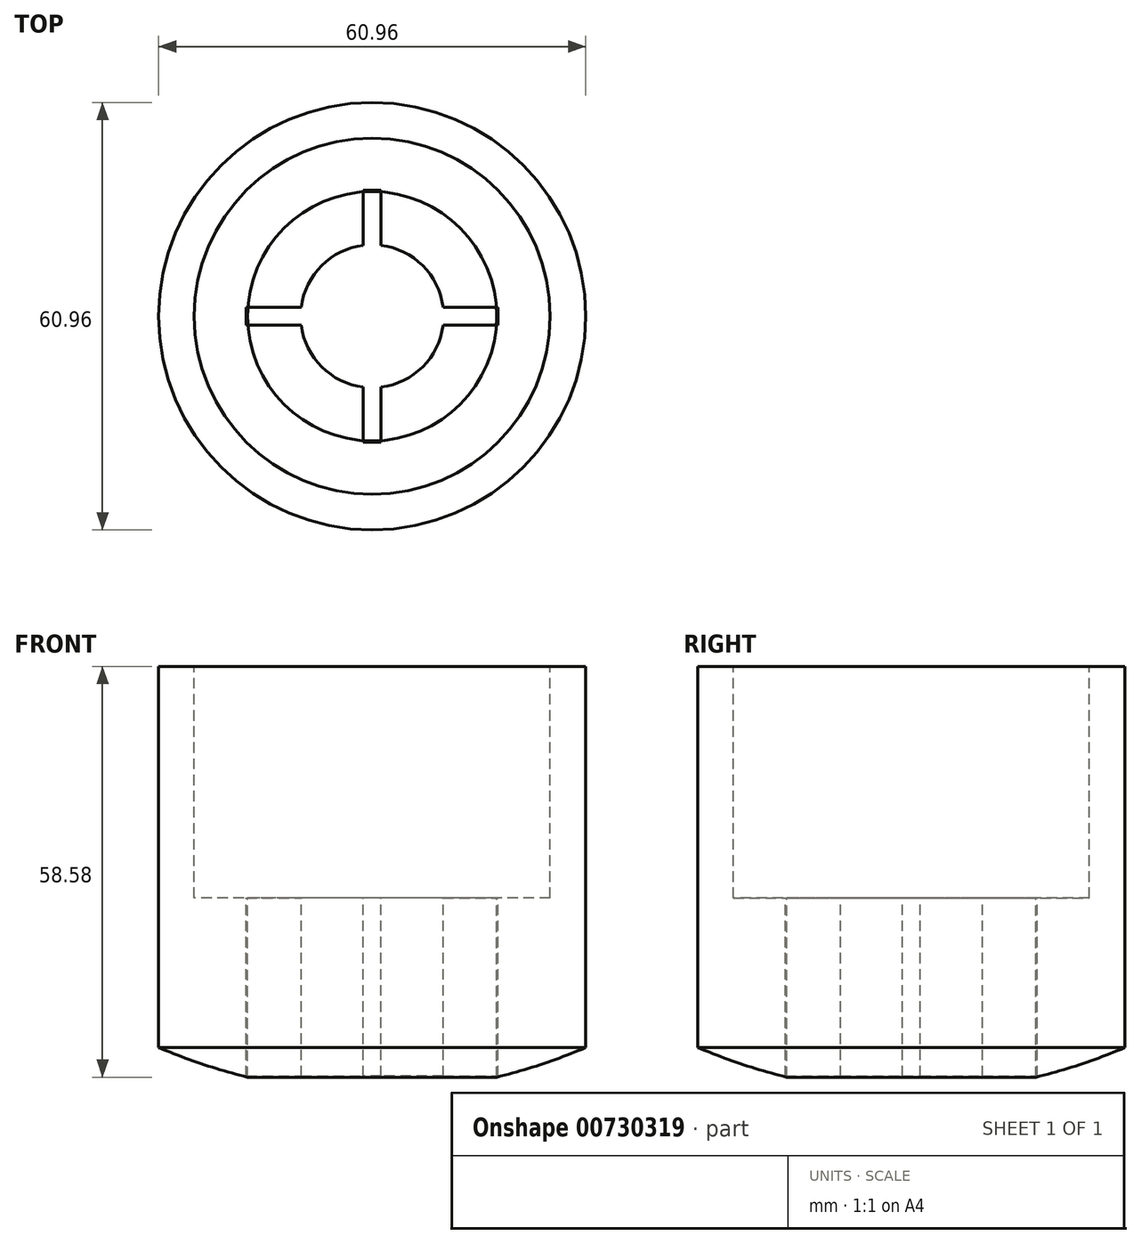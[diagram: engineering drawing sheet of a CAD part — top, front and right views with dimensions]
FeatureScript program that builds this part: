
annotation { "Feature Type Name" : "Feature", "Feature Type Description" : "" }
export const myFeature = defineFeature(function(context is Context, id is Id, definition is map)
    precondition{}
    {
        {
            var Q0;
            Q0=qCreatedBy(makeId("Front.planeOp"),FACE);
            var sketch = newSketch(context, id + "F0", { "sketchPlane" : qUnion([Q0])});
            skLineSegment(sketch, "E0", {"start": v(0, 60.96) * mm, "end": v(0, 0) * mm});
            skLineSegment(sketch, "E1", {"start": v(0, 60.96) * mm, "end": v(30.48, 60.96) * mm});
            skLineSegment(sketch, "E2", {"start": v(30.48, 60.96) * mm, "end": v(30.48, 6.61) * mm});
            skArc(sketch, "E3", {"start": v(0, 0) * mm, "mid": v(15.55, 1.86) * mm, "end": v(30.48, 6.61) * mm});
            skSolve(sketch);
        }
        {
            var Q0;
            Q0=makeQuery(id+"F0.imprint","IMPRINT",FACE,{"disambiguationData":[TD([[makeQuery(id+"F0.imprint","IMPRINT",EDGE,{"derivedFrom":sQuery(id+"F0.wireOp",EDGE,"E0")}),1.0]])]});
            var Q1;
            Q1 = qSketchRegion(id + "F2", true);
            var Q2;
            Q2=sQuery(id+"F0.wireOp",EDGE,"E0");
            revolve(context, id + "F1", {"surfaceOperationType" : NewSurfaceOperationType.NEW, "entities" : qUnion([Q0, Q1]), "axis" : qUnion([Q2]), "revolveType" : RevolveType.FULL});
        }
        {
            var Q0;
            Q0=makeQuery(id+"F1.opRevolve","SWEPT_FACE",FACE,{"disambiguationData":[OSD([sQuery(id+"F0.wireOp",EDGE,"E1")])]});
            var sketch = newSketch(context, id + "F2", { "sketchPlane" : qUnion([Q0])});
            skCircle(sketch, "E4", {"center": v(0, 0) * mm, "radius": 25.4 * mm});
            skCircle(sketch, "E5", {"center": v(0, 0) * mm, "radius": 17.78 * mm});
            skSolve(sketch);
        }
        {
            var Q0;
            Q0 = qSketchRegion(id + "F2", true);
            extrude(context, id + "F3", {"entities" : qUnion([Q0]), "operationType" : NewBodyOperationType.REMOVE, "oppositeDirection" : true, "depth" : 33.02 * mm, "offsetDistance" : 25.4 * mm});
        }
        {
            var Q0;
            Q0=makeQuery(id+"F3.boolean.opBoolean","SPLIT",FACE,{"disambiguationData":[TD([makeQuery(id+"F3.opExtrude","SWEPT_FACE",FACE,{"disambiguationData":[OSD([sQuery(id+"F2.wireOp",EDGE,"E5")])]})])],"derivedFrom":makeQuery(id+"F1.opRevolve","SWEPT_FACE",FACE,{"disambiguationData":[OSD([sQuery(id+"F0.wireOp",EDGE,"E1")])]})});
            extrude(context, id + "F4", {"entities" : qUnion([Q0]), "operationType" : NewBodyOperationType.REMOVE, "oppositeDirection" : true, "depth" : 60.96 * mm, "offsetDistance" : 25.4 * mm});
        }
        {
            var Q0;
            Q0=makeQuery(id+"F3.boolean.opBoolean","COPY",FACE,{"derivedFrom":makeQuery(id+"F3.opExtrude","CAP_FACE",FACE,{"disambiguationData":[OSD([sQuery(id+"F2.wireOp",EDGE,"E4"),sQuery(id+"F2.wireOp",EDGE,"E5")])],"isStart":false})});
            var sketch = newSketch(context, id + "F5", { "sketchPlane" : qUnion([Q0])});
            skLineSegment(sketch, "E6.bottom", {"start": v(1.27, -17.96) * mm, "end": v(-1.27, -17.96) * mm});
            skLineSegment(sketch, "E6.top", {"start": v(1.27, 17.96) * mm, "end": v(-1.27, 17.96) * mm});
            skLineSegment(sketch, "E6.left", {"start": v(1.27, -17.96) * mm, "end": v(1.27, 17.96) * mm});
            skLineSegment(sketch, "E6.right", {"start": v(-1.27, -17.96) * mm, "end": v(-1.27, 17.96) * mm});
            skPoint(sketch, "E6.middle", {"position": v(0, 0) * mm});
            skLineSegment(sketch, "E7.bottom", {"start": v(-17.97, -1.27) * mm, "end": v(17.97, -1.27) * mm});
            skLineSegment(sketch, "E7.top", {"start": v(-17.97, 1.27) * mm, "end": v(17.97, 1.27) * mm});
            skLineSegment(sketch, "E7.left", {"start": v(-17.97, -1.27) * mm, "end": v(-17.97, 1.27) * mm});
            skLineSegment(sketch, "E7.right", {"start": v(17.97, -1.27) * mm, "end": v(17.97, 1.27) * mm});
            skSolve(sketch);
        }
        {
            var Q0;
            Q0 = qSketchRegion(id + "F5", true);
            extrude(context, id + "F6", {"entities" : qUnion([Q0]), "oppositeDirection" : true, "depth" : 25.43 * mm, "offsetDistance" : 25.4 * mm});
        }
        {
            var Q0;
            Q0=makeQuery(id+"F6.opExtrude","CAP_FACE",FACE,{"disambiguationData":[OSD([sQuery(id+"F5.wireOp",EDGE,"E6.bottom"),sQuery(id+"F5.wireOp",EDGE,"E6.top"),sQuery(id+"F5.wireOp",EDGE,"E6.left"),sQuery(id+"F5.wireOp",EDGE,"E6.right"),sQuery(id+"F5.wireOp",EDGE,"E7.bottom"),sQuery(id+"F5.wireOp",EDGE,"E7.top"),sQuery(id+"F5.wireOp",EDGE,"E7.left"),sQuery(id+"F5.wireOp",EDGE,"E7.right")])],"isStart":true});
            var sketch = newSketch(context, id + "F7", { "sketchPlane" : qUnion([Q0])});
            skLineSegment(sketch, "E8", {"start": v(0, -17.82) * mm, "end": v(0, -10.2) * mm});
            skCircle(sketch, "E9", {"center": v(0, 0) * mm, "radius": 10.2 * mm});
            skSolve(sketch);
        }
        {
            var Q0;
            Q0 = qSketchRegion(id + "F7", true);
            extrude(context, id + "F8", {"entities" : qUnion([Q0]), "operationType" : NewBodyOperationType.ADD, "oppositeDirection" : true, "depth" : 25.43 * mm, "offsetDistance" : 25.4 * mm});
        }
    });
